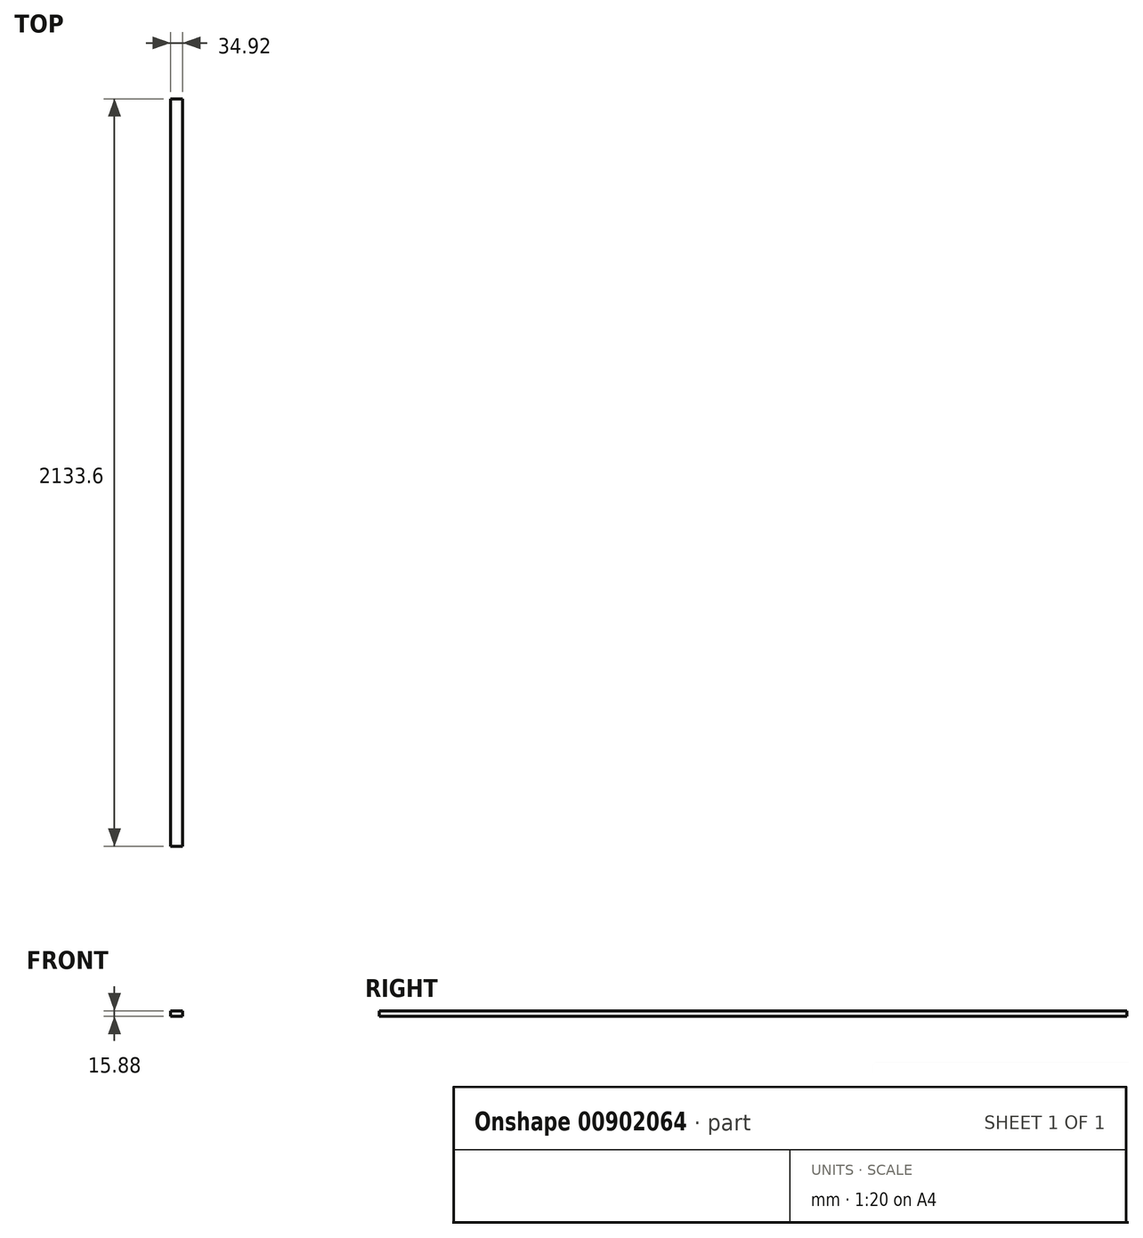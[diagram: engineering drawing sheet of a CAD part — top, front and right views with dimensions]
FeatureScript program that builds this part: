
annotation { "Feature Type Name" : "Feature", "Feature Type Description" : "" }
export const myFeature = defineFeature(function(context is Context, id is Id, definition is map)
    precondition{}
    {
        {
            var Q0;
            Q0=qCreatedBy(makeId("Front.planeOp"),FACE);
            var sketch = newSketch(context, id + "F0", { "sketchPlane" : qUnion([Q0])});
            skLineSegment(sketch, "E0.bottom", {"start": v(0, 0) * mm, "end": v(34.93, 0) * mm});
            skLineSegment(sketch, "E0.top", {"start": v(0, 15.88) * mm, "end": v(34.93, 15.88) * mm});
            skLineSegment(sketch, "E0.left", {"start": v(0, 0) * mm, "end": v(0, 15.88) * mm});
            skLineSegment(sketch, "E0.right", {"start": v(34.93, 0) * mm, "end": v(34.93, 15.88) * mm});
            skSolve(sketch);
        }
        {
            var Q0;
            Q0=makeQuery(id+"F0.imprint","IMPRINT",FACE,{"disambiguationData":[TD([[makeQuery(id+"F0.imprint","IMPRINT",EDGE,{"derivedFrom":sQuery(id+"F0.wireOp",EDGE,"E0.bottom")}),1.0]])]});
            extrude(context, id + "F1", {"entities" : qUnion([Q0]), "depth" : 2133.6 * mm, "offsetDistance" : 25.4 * mm});
        }
    });
